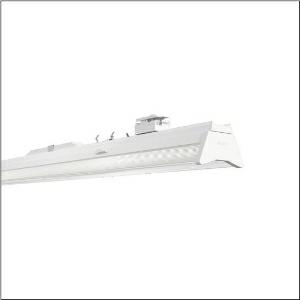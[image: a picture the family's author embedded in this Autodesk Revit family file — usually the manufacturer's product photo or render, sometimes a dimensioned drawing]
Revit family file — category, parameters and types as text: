
# Revit family: licross_r__21_performance_mo_51td16vn445g_3318
name_source: partatom
category: Lighting Fixtures
units: mm (PartAtom-declared; Revit-internal decimal feet)

## family parameters
Cut with Voids When Loaded = No
Host = Face
Light Source = No
Part Type = Normal
Room Calculation Point = No
Round Connector Dimension = Use Diameter
Shared = No

## types (1)
- --- (1 x LED, 4500 lm, 24.2 W, 4000K)
    Apparent Load = 24 VA
    CIE Flux Codes = 66 88 96 79 100
    Color Rendering = 80
    Color Temperature = 4000K
    Default Elevation = 1800 mm
    Description = Licross® 21 Performance MO, luminaire insert, of sheet steel, galvanised, coil coated, white, length: 1.500mm, width: 120mm, height: 123mm, LED rated luminous flux: 4.500lm, light colour: 840, control gear: DALI 2, CLO, with plug, 5-pole, with phase selection, mains connection: 220..240V, AC, 50/60Hz, start of lifetime: 24W, end of service life: 26W, halogen-free wiring, primary light control with lens, of plastic, primary optical cover: cover, of PMMA, light emission: direct/indirect distribution, primary light characteristic: symmetric, protection rating (complete): IP54, insulation class (complete): insulation class I (protective earthing), certification: CE, ENEC, VDE, UKCA, protection symbol: D if used in an environment with non-conductive dust loads with corresponding accessories, impact resistance: IK06, permissible ambient temperature for indoor applications: -25..+45°C, corresponds to IFS (International Featured Standards) requirements for safety and quality in the food industry, reducing of maximum allowable ambient temperature of 5°C with ceiling mounting, LABS conformity tested according to VDMA 24364:2018-05, packaging unit: 1 piece
    Height = 114 mm
    Lamp = 1 x LED
    Lamp Light Flux = 4500 lm
    Lamp Power = 24.2 W
    Lamp count = 1
    Length = 1500 mm
    Luminous efficacy = 186 lm/W
    Manufacturer = Siteco
    ModVariant = No
    Model = 51TD16VN445G
    Mounting Place = Ceiling
    Mounting Type = Pendant
    Number of Poles = 1
    OnlyDefault = Yes
    Power Factor = 1
    Product Name = Licross® 21 Performance MO
    Product group = luminaire insert
    ProductGroupID = 902
    Protection Class = Protection class I
    Protection Degree = IP 54
    RLX_Detail_Level = 1
    RLX_Emergency_Light_Flux = 0 lm
    RLX_Emergency_Type = 0
    RLX_Emergency_Type_DB = No
    RlxData = <blob elided: 33737 chars, md5=79488291>
    Socket = socket
    Standby Power = 0 W
    System Light Flux = 4500 lm
    System Power = 24 W
    Type Comments = factory setting: luminous flux: 100 % | dim-lin: 254 | 160 mA
    Type Image = l_1256138.jpg
    URL = http://relux.com
    VarID = @adj_049418
    Voltage = 0 V
    Weight = 0.00 kg
    Width = 120 mm

## geometry (parser evidence)
native form markers: Blend x4, Sweep x11
no freeform markers — native parametric forms only
